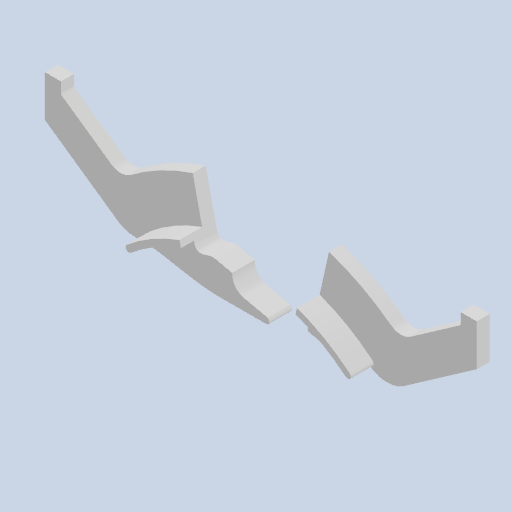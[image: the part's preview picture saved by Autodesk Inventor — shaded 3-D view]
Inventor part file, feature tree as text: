
AUTODESK INVENTOR PART (.ipt)
format: ipt  version: 2022 (Build 260153000, 153)  size: 288,768 bytes
history: native  units: mm
features: reference x16, other x6, extrude x3, sketch x3, fillet x2, projected_geometry x2
ambient origin geometry x8: Origin, YZ Plane, XZ Plane, XY Plane, X Axis, Y Axis, Z Axis, Center Point
bodies: Body1 (feature_tree)
feature tree (32):
  other  "Твердое тело1"
  extrude  "Выдавливание1"  Depth=9.0mm
  extrude  "Выдавливание2"  Depth=4.0mm TaperAngle=0.0deg
  extrude  "Выдавливание3"  Depth=9.0mm
  fillet  "Сопряжение1"  Radius=7.0mm
  fillet  "Сопряжение2"  Radius=2.0mm
  sketch  "Эскиз1"
  reference  "Ссылка1"
  reference  "Ссылка2"
  reference  "Ссылка3"
  reference  "Ссылка4"
  reference  "Ссылка5"
  reference  "Ссылка6"
  reference  "Ссылка7"
  reference  "Ссылка8"
  reference  "Ссылка9"
  reference  "Ссылка10"
  sketch  "Эскиз2"
  sketch  "Эскиз3"
  projected_geometry  "Спроецированная петля1"
  projected_geometry  "Спроецированная петля2"
  reference  "Ссылка11"
  reference  "Ссылка12"
  reference  "Ссылка13"
  reference  "Ссылка14"
  reference  "Ссылка15"
  reference  "Ссылка16"
  other  "<userpath>\Documents\Git\MZCAT_2024\MZCAT.iam"
  other  "MZCAT.iam"
  other  "vydacha_backstenka:1"
  other  "OCS-D008 B:1"
  other  "magazine:1"
